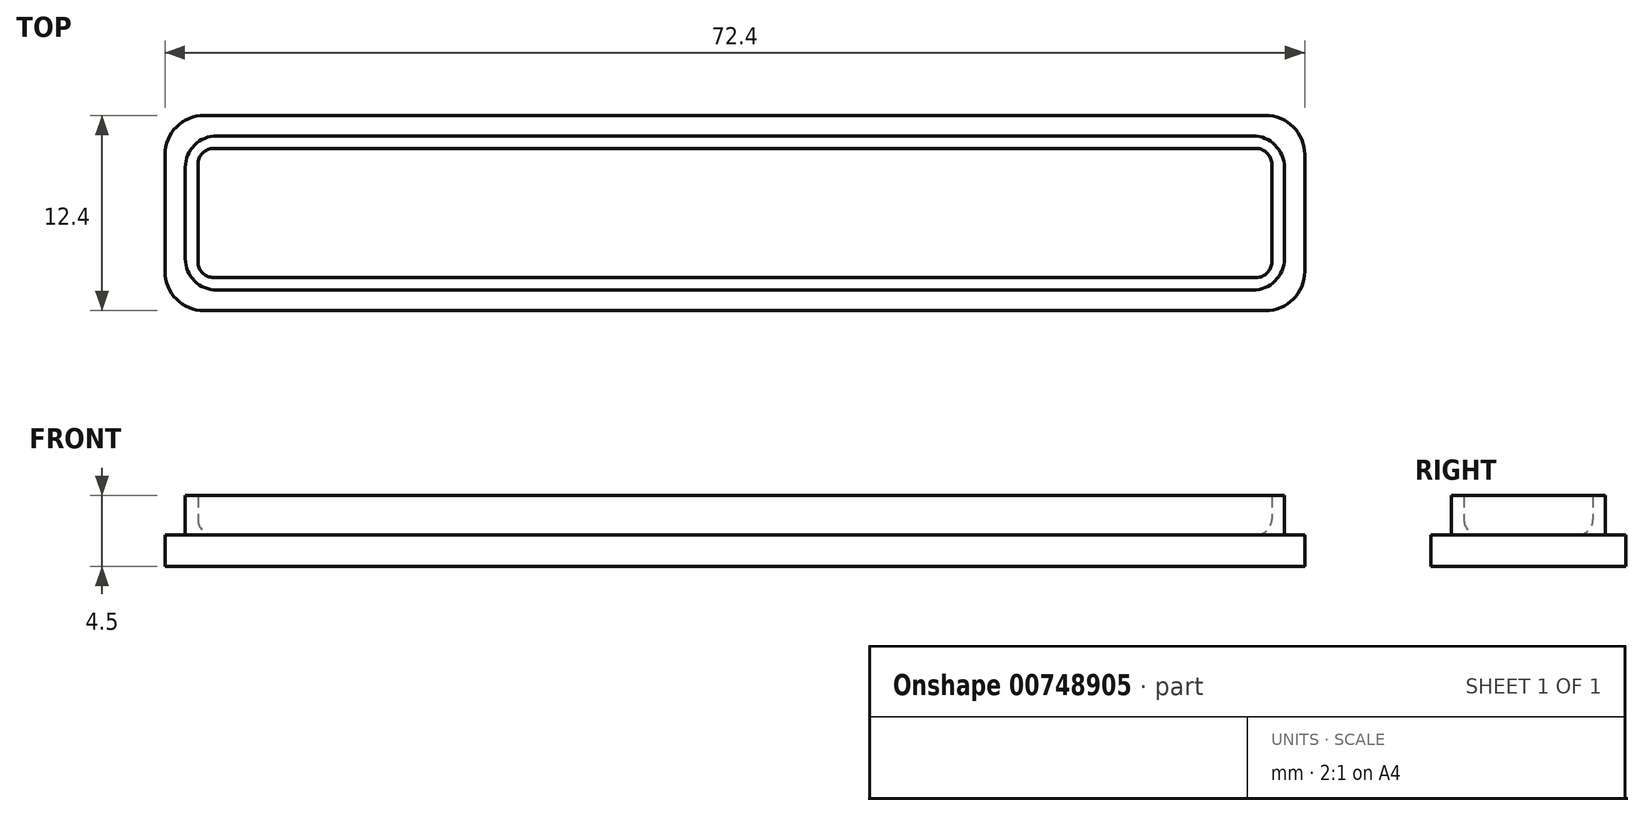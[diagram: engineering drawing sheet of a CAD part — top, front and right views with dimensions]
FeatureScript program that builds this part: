
annotation { "Feature Type Name" : "Feature", "Feature Type Description" : "" }
export const myFeature = defineFeature(function(context is Context, id is Id, definition is map)
    precondition{}
    {
        {
            var Q0;
            Q0=qCreatedBy(makeId("Top.planeOp"),FACE);
            var sketch = newSketch(context, id + "F0", { "sketchPlane" : qUnion([Q0])});
            skLineSegment(sketch, "E0.bottom", {"start": v(-15.43, 12.97) * mm, "end": v(54.37, 12.97) * mm});
            skLineSegment(sketch, "E0.top", {"start": v(-15.43, 3.17) * mm, "end": v(54.37, 3.17) * mm});
            skLineSegment(sketch, "E0.left", {"start": v(-15.43, 12.97) * mm, "end": v(-15.43, 3.17) * mm});
            skLineSegment(sketch, "E0.right", {"start": v(54.37, 12.97) * mm, "end": v(54.37, 3.17) * mm});
            skLineSegment(sketch, "E1.0", {"start": v(-16.73, 14.27) * mm, "end": v(55.67, 14.27) * mm});
            skLineSegment(sketch, "E1.1", {"start": v(-16.73, 14.27) * mm, "end": v(-16.73, 1.87) * mm});
            skLineSegment(sketch, "E1.2", {"start": v(-16.73, 1.87) * mm, "end": v(55.67, 1.87) * mm});
            skLineSegment(sketch, "E1.3", {"start": v(55.67, 14.27) * mm, "end": v(55.67, 1.87) * mm});
            skLineSegment(sketch, "E2.0", {"start": v(-14.63, 12.17) * mm, "end": v(53.57, 12.17) * mm});
            skLineSegment(sketch, "E2.1", {"start": v(-14.63, 12.17) * mm, "end": v(-14.63, 3.97) * mm});
            skLineSegment(sketch, "E2.2", {"start": v(-14.63, 3.97) * mm, "end": v(53.57, 3.97) * mm});
            skLineSegment(sketch, "E2.3", {"start": v(53.57, 12.17) * mm, "end": v(53.57, 3.97) * mm});
            skSolve(sketch);
        }
        {
            var Q0;
            Q0=makeQuery(id+"F0.imprint","IMPRINT",FACE,{"disambiguationData":[TD([[makeQuery(id+"F0.imprint","IMPRINT",EDGE,{"derivedFrom":sQuery(id+"F0.wireOp",EDGE,"E0.bottom")}),-1.0]])]});
            var Q1;
            Q1=makeQuery(id+"F0.imprint","IMPRINT",FACE,{"disambiguationData":[TD([[makeQuery(id+"F0.imprint","IMPRINT",EDGE,{"derivedFrom":sQuery(id+"F0.wireOp",EDGE,"E0.bottom")}),1.0]])]});
            var Q2;
            Q2=makeQuery(id+"F0.imprint","IMPRINT",FACE,{"disambiguationData":[TD([[makeQuery(id+"F0.imprint","IMPRINT",EDGE,{"derivedFrom":sQuery(id+"F0.wireOp",EDGE,"E2.0")}),-1.0]])]});
            extrude(context, id + "F1", {"entities" : qUnion([Q0, Q1, Q2]), "oppositeDirection" : true, "depth" : 2 * mm, "offsetDistance" : 25 * mm});
        }
        {
            var Q0;
            Q0=makeQuery(id+"F0.imprint","IMPRINT",FACE,{"disambiguationData":[TD([[makeQuery(id+"F0.imprint","IMPRINT",EDGE,{"derivedFrom":sQuery(id+"F0.wireOp",EDGE,"E0.bottom")}),-1.0]])]});
            extrude(context, id + "F2", {"entities" : qUnion([Q0]), "operationType" : NewBodyOperationType.ADD, "depth" : 2.5 * mm, "offsetDistance" : 25 * mm});
        }
        {
            var Q0;
            Q0=makeQuery(id+"F1.opExtrude","SWEPT_EDGE",EDGE,{"disambiguationData":[OSD([sQuery(id+"F0.wireOp",EDGE,"E1.0"),sQuery(id+"F0.wireOp",EDGE,"E1.1")])]});
            var Q1;
            Q1=makeQuery(id+"F1.opExtrude","SWEPT_EDGE",EDGE,{"disambiguationData":[OSD([sQuery(id+"F0.wireOp",EDGE,"E1.1"),sQuery(id+"F0.wireOp",EDGE,"E1.2")])]});
            var Q2;
            Q2=makeQuery(id+"F1.opExtrude","SWEPT_EDGE",EDGE,{"disambiguationData":[OSD([sQuery(id+"F0.wireOp",EDGE,"E1.0"),sQuery(id+"F0.wireOp",EDGE,"E1.3")])]});
            var Q3;
            Q3=makeQuery(id+"F1.opExtrude","SWEPT_EDGE",EDGE,{"disambiguationData":[OSD([sQuery(id+"F0.wireOp",EDGE,"E1.2"),sQuery(id+"F0.wireOp",EDGE,"E1.3")])]});
            fillet(context, id + "F3", {"entities" : qUnion([Q0, Q1, Q2, Q3]), "radius" : 2.5 * mm, "tangentPropagation" : true, "allowEdgeOverflow" : false});
        }
        {
            var Q0;
            Q0=makeQuery(id+"F2.opExtrude","SWEPT_EDGE",EDGE,{"disambiguationData":[OSD([sQuery(id+"F0.wireOp",EDGE,"E0.bottom"),sQuery(id+"F0.wireOp",EDGE,"E0.right")])]});
            var Q1;
            Q1=makeQuery(id+"F2.opExtrude","SWEPT_EDGE",EDGE,{"disambiguationData":[OSD([sQuery(id+"F0.wireOp",EDGE,"E0.top"),sQuery(id+"F0.wireOp",EDGE,"E0.right")])]});
            var Q2;
            Q2=makeQuery(id+"F2.opExtrude","SWEPT_EDGE",EDGE,{"disambiguationData":[OSD([sQuery(id+"F0.wireOp",EDGE,"E0.bottom"),sQuery(id+"F0.wireOp",EDGE,"E0.left")])]});
            var Q3;
            Q3=makeQuery(id+"F2.opExtrude","SWEPT_EDGE",EDGE,{"disambiguationData":[OSD([sQuery(id+"F0.wireOp",EDGE,"E0.top"),sQuery(id+"F0.wireOp",EDGE,"E0.left")])]});
            fillet(context, id + "F4", {"entities" : qUnion([Q0, Q1, Q2, Q3]), "radius" : 2 * mm, "tangentPropagation" : true, "allowEdgeOverflow" : false});
        }
        {
            var Q0;
            Q0=makeQuery(id+"F2.opExtrude","SWEPT_EDGE",EDGE,{"disambiguationData":[OSD([sQuery(id+"F0.wireOp",EDGE,"E2.2"),sQuery(id+"F0.wireOp",EDGE,"E2.3")])]});
            var Q1;
            Q1=makeQuery(id+"F2.opExtrude","SWEPT_EDGE",EDGE,{"disambiguationData":[OSD([sQuery(id+"F0.wireOp",EDGE,"E2.0"),sQuery(id+"F0.wireOp",EDGE,"E2.3")])]});
            var Q2;
            Q2=makeQuery(id+"F2.opExtrude","SWEPT_EDGE",EDGE,{"disambiguationData":[OSD([sQuery(id+"F0.wireOp",EDGE,"E2.1"),sQuery(id+"F0.wireOp",EDGE,"E2.2")])]});
            var Q3;
            Q3=makeQuery(id+"F2.opExtrude","SWEPT_EDGE",EDGE,{"disambiguationData":[OSD([sQuery(id+"F0.wireOp",EDGE,"E2.0"),sQuery(id+"F0.wireOp",EDGE,"E2.1")])]});
            fillet(context, id + "F5", {"entities" : qUnion([Q0, Q1, Q2, Q3]), "radius" : 1 * mm, "tangentPropagation" : true, "allowEdgeOverflow" : false});
        }
        {
            var Q0;
            Q0=makeQuery(id+"F2.opExtrude","CAP_EDGE",EDGE,{"disambiguationData":[OSD([sQuery(id+"F0.wireOp",EDGE,"E2.0")])],"isStart":true});
            var Q1;
            Q1=makeQuery(id+"F2.opExtrude","CAP_EDGE",EDGE,{"disambiguationData":[OSD([sQuery(id+"F0.wireOp",EDGE,"E2.3")])],"isStart":true});
            var Q2;
            Q2=makeQuery(id+"F2.opExtrude","CAP_EDGE",EDGE,{"disambiguationData":[OSD([sQuery(id+"F0.wireOp",EDGE,"E2.2")])],"isStart":true});
            var Q3;
            Q3=makeQuery(id+"F2.opExtrude","CAP_EDGE",EDGE,{"disambiguationData":[OSD([sQuery(id+"F0.wireOp",EDGE,"E2.1")])],"isStart":true});
            fillet(context, id + "F6", {"entities" : qUnion([Q0, Q1, Q2, Q3]), "radius" : 1 * mm, "tangentPropagation" : true, "allowEdgeOverflow" : false});
        }
    });
